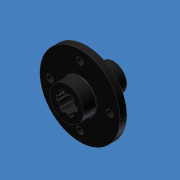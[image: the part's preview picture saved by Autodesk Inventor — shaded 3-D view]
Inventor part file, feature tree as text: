
AUTODESK INVENTOR PART (.ipt)
format: ipt  version: 2012 (Build 160160000, 160)  size: 178,688 bytes
history: native  units: mm (DEFAULTED — no unit token found)
features: sketch x8, extrude x5, hole x3, pattern_circular x2, fillet x1
ambient origin geometry x8: Origin, YZ Plane, XZ Plane, XY Plane, X Axis, Y Axis, Z Axis, Center Point
bodies: Solid1 (feature_tree)
feature tree (19):
  extrude  "Extrusion1"  Depth=76.2mm
  hole  "Mounting Hole"  [1 undecoded]
  pattern_circular  "Circular Pattern1"  Count=4 Angle=360.0deg
  extrude  "Extrusion2"  Depth=12.7mm TaperAngle=0.0deg
  hole  "Hole3"  [1 undecoded]
  extrude  "Extrusion3"  Depth=25.4mm
  pattern_circular  "Circular Pattern2"  [2 undecoded]
  extrude  "Extrusion4"  Depth=28.575mm TaperAngle=0.0deg
  extrude  "Extrusion5"  Depth=0.508mm
  hole  "Hole2"  [1 undecoded]
  fillet  "Fillet1"  Radius=4.0mm
  sketch  "Sketch1"  dims[d0=6.35mm d1=0.0mm d2=76.2mm]
  sketch  "Sketch2"  dims[d3=0.0mm d4=28.575mm]
  sketch  "Sketch3"  dims[d5=6.35mm d6=12.7mm d7=9.525mm d8=6.35mm d9=14.3117mm d10=19.05mm d11=20.594885mm d12=40.0mm d14=360.0deg]
  sketch  "Sketch4"  dims[d15=31.75mm d17=12.7mm d18=0.0mm]
  sketch  "Sketch5"  dims[d22=12.7mm d23=0.0mm d24=60.0mm d26=360.0deg]
  sketch  "Sketch6"  dims[d27=29.845mm d28=25.4mm d29=-0.872665mm]
  sketch  "Sketch7"  dims[d31=16.0mm]
  sketch  "Sketch8"  dims[d32=4.7625mm d33=10.31875mm d34=28.575mm d35=0.0mm d36=9.525mm d37=12.7mm d38=9.525mm d39=6.35mm d40=14.3117mm d41=19.05mm d42=20.594885mm d43=0.508mm d46=60.0deg d47=4.0mm d48=20.0mm d49=16.2mm d50=12.7mm d51=9.525mm d52=6.35mm d53=14.3117mm d54=14.986mm d55=0.0mm]
note: 5 required parameter values undecoded (feature->parameter linkage not recoverable at this tier; creation-order binding heuristic only, values carry confidence <= 0.55)
